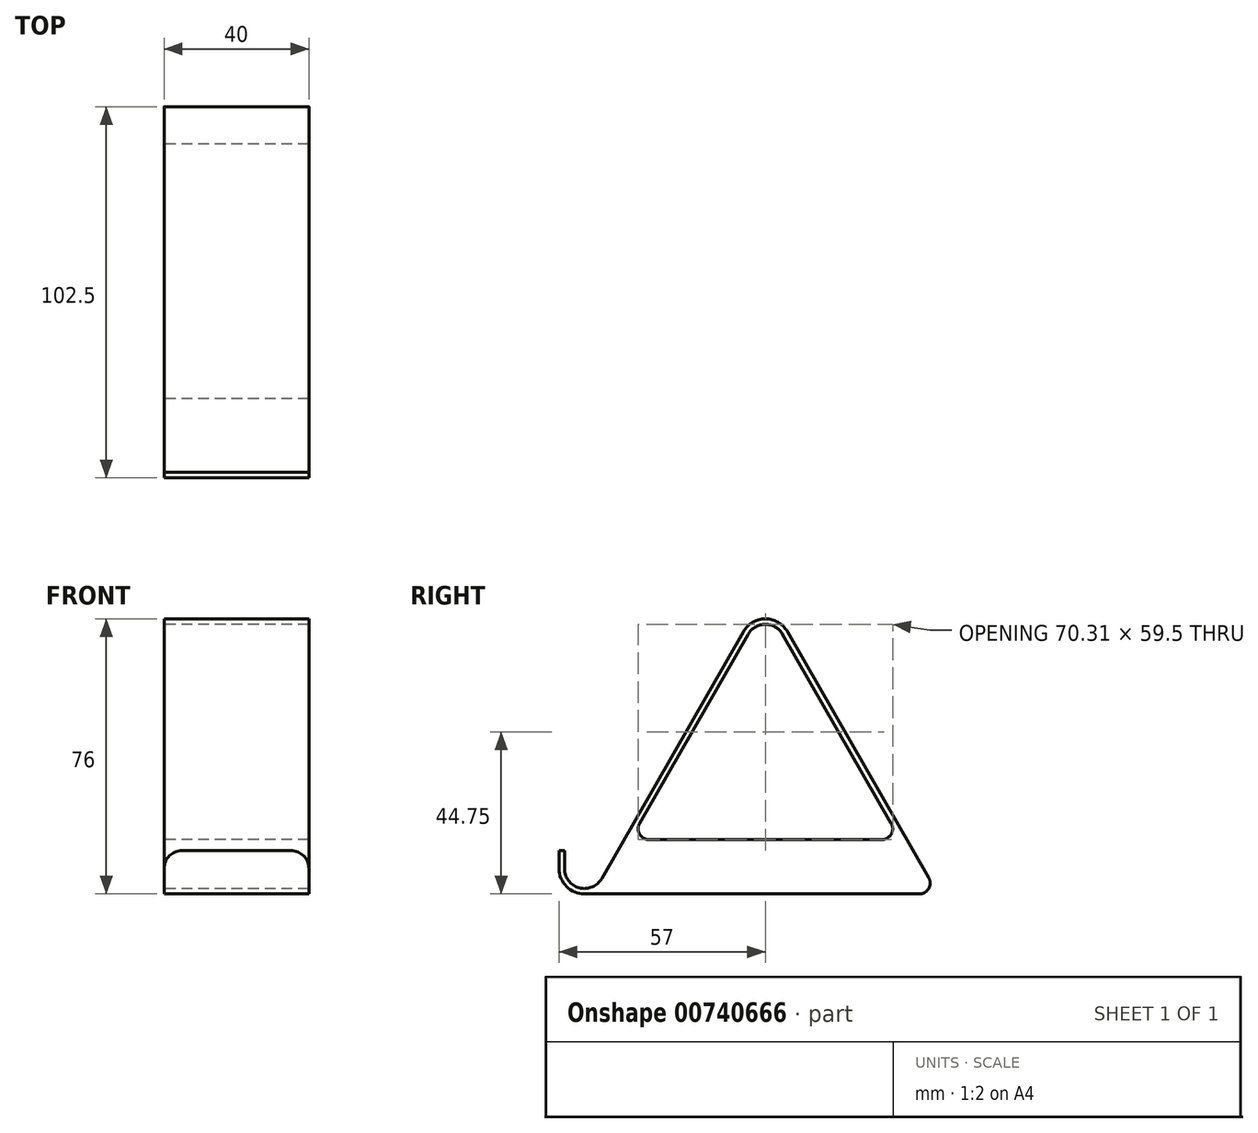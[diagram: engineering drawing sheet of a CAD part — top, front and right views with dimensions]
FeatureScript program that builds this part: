
annotation { "Feature Type Name" : "Feature", "Feature Type Description" : "" }
export const myFeature = defineFeature(function(context is Context, id is Id, definition is map)
    precondition{}
    {
        {
            var Q0;
            Q0=qCreatedBy(makeId("Right.planeOp"),FACE);
            var sketch = newSketch(context, id + "F0", { "sketchPlane" : qUnion([Q0])});
            skArc(sketch, "E0", {"start": v(-7, 0) * mm, "mid": v(-4.95, -4.95) * mm, "end": v(0, -7) * mm});
            skArc(sketch, "E1", {"start": v(54.77, 64.74) * mm, "mid": v(50, 67.5) * mm, "end": v(45.23, 64.74) * mm});
            skLineSegment(sketch, "E2", {"start": v(15.24, 12.5) * mm, "end": v(45.23, 64.74) * mm});
            skLineSegment(sketch, "E3", {"start": v(50, 62) * mm, "end": v(50, -2.18) * mm, "construction": true});
            skLineSegment(sketch, "E4", {"start": v(0, -7) * mm, "end": v(92.5, -7) * mm, "construction": true});
            skPoint(sketch, "E5.orphan", {"position": v(93.93, -3.48) * mm});
            skLineSegment(sketch, "E6", {"start": v(-7, 0) * mm, "end": v(-7, 5) * mm});
            skLineSegment(sketch, "E7.0", {"start": v(-5.5, 0) * mm, "end": v(-5.5, 5) * mm});
            skLineSegment(sketch, "E7.1", {"start": v(95.1, -2.5) * mm, "end": v(56.07, 65.48) * mm});
            skArc(sketch, "E7.2", {"start": v(56.07, 65.48) * mm, "mid": v(50, 69) * mm, "end": v(43.93, 65.48) * mm});
            skLineSegment(sketch, "E7.3", {"start": v(4.77, -2.74) * mm, "end": v(43.93, 65.48) * mm});
            skArc(sketch, "E7.4", {"start": v(-5.5, 0) * mm, "mid": v(-1.42, -5.31) * mm, "end": v(4.77, -2.74) * mm});
            skLineSegment(sketch, "E8", {"start": v(0, -7) * mm, "end": v(97.68, -7) * mm});
            skLineSegment(sketch, "E9.0", {"start": v(17.84, 8) * mm, "end": v(82.16, 8) * mm});
            skLineSegment(sketch, "E10", {"start": v(-7, 5) * mm, "end": v(-5.5, 5) * mm});
            skPoint(sketch, "E11.orphan", {"position": v(6.07, -3.48) * mm});
            skLineSegment(sketch, "E12.trimOffspring", {"start": v(84.76, 12.5) * mm, "end": v(54.77, 64.74) * mm});
            skPoint(sketch, "E13.visualSharp", {"position": v(12.66, 8) * mm});
            skArc(sketch, "E13.filletArc", {"start": v(15.24, 12.5) * mm, "mid": v(15.25, 9.5) * mm, "end": v(17.84, 8) * mm});
            skPoint(sketch, "E14.visualSharp", {"position": v(87.34, 8) * mm});
            skArc(sketch, "E14.filletArc", {"start": v(82.16, 8) * mm, "mid": v(84.75, 9.5) * mm, "end": v(84.76, 12.5) * mm});
            skArc(sketch, "E15.filletArc", {"start": v(92.5, -7) * mm, "mid": v(95.1, -5.5) * mm, "end": v(95.1, -2.5) * mm});
            skSolve(sketch);
        }
        {
            var Q0;
            {var subQ1=sQuery(id+"F0.wireOp",EDGE,"E0");Q0=makeQuery(id+"F0.imprint","IMPRINT",FACE,{"disambiguationData":[TD([[makeQuery(id+"F0.imprint","IMPRINT",EDGE,{"derivedFrom":subQ1}),1.0]])]});}
            extrude(context, id + "F1", {"entities" : qUnion([Q0]), "depth" : 40 * mm, "offsetDistance" : 25 * mm});
        }
        {
            var Q0;
            Q0=makeQuery(id+"F1.opExtrude","CAP_EDGE",EDGE,{"disambiguationData":[OSD([sQuery(id+"F0.wireOp",EDGE,"E10")])],"isStart":false});
            var Q1;
            Q1=makeQuery(id+"F1.opExtrude","CAP_EDGE",EDGE,{"disambiguationData":[OSD([sQuery(id+"F0.wireOp",EDGE,"E10")])],"isStart":true});
            fillet(context, id + "F2", {"entities" : qUnion([Q0, Q1]), "radius" : 5 * mm, "tangentPropagation" : true, "allowEdgeOverflow" : false});
        }
    });
